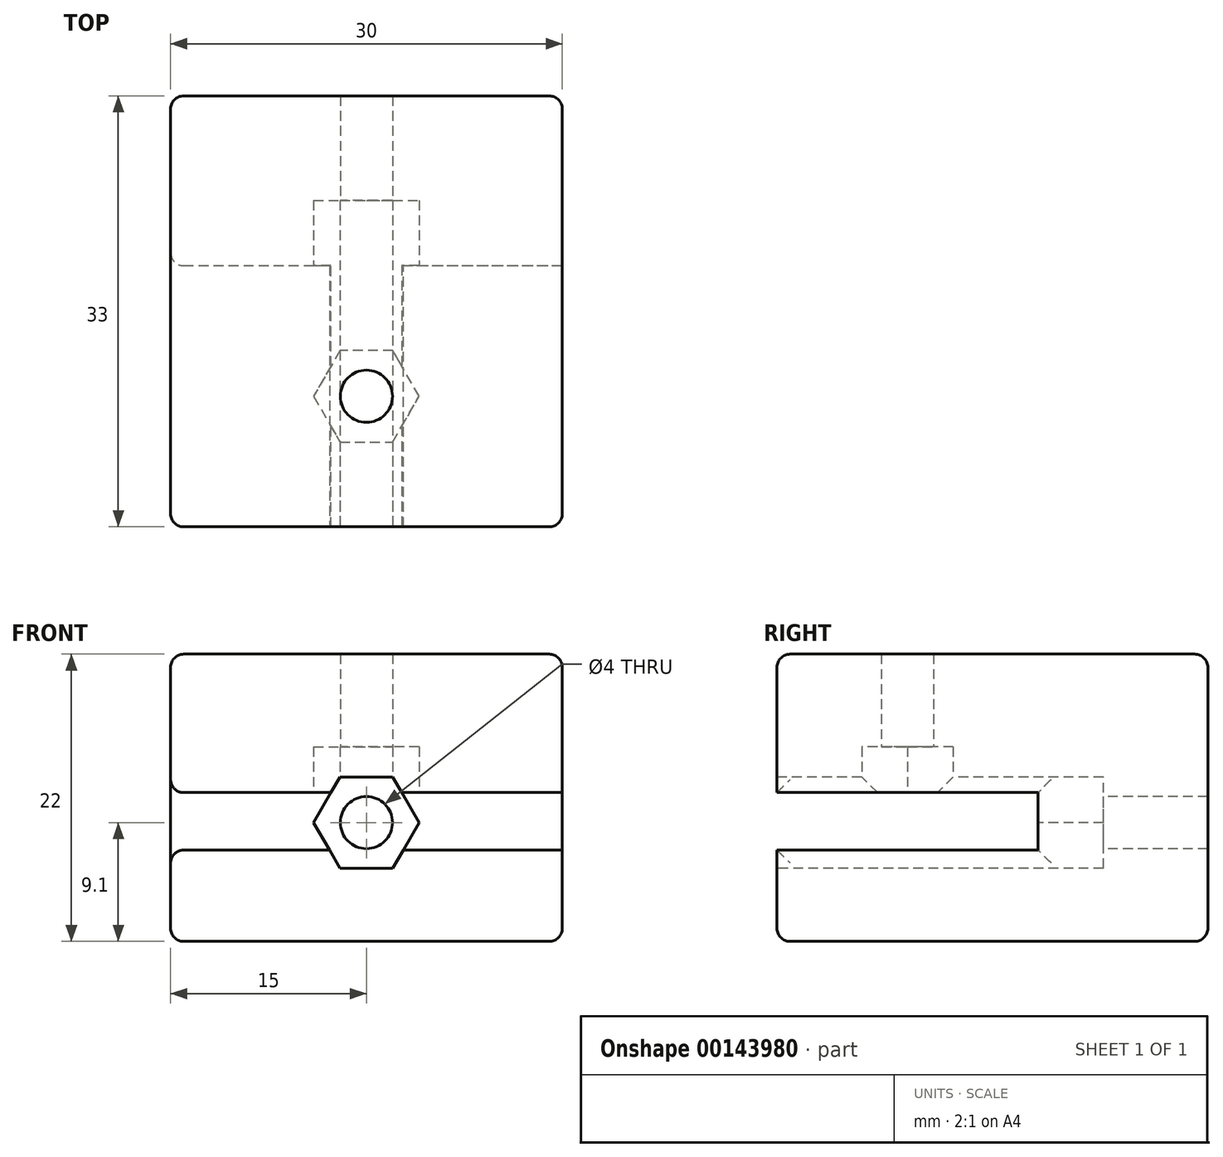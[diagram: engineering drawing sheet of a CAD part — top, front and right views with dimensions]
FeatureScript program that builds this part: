
annotation { "Feature Type Name" : "Feature", "Feature Type Description" : "" }
export const myFeature = defineFeature(function(context is Context, id is Id, definition is map)
    precondition{}
    {
        {
            var Q0;
            Q0=qCreatedBy(makeId("Top.planeOp"),FACE);
            var sketch = newSketch(context, id + "F0", { "sketchPlane" : qUnion([Q0])});
            skLineSegment(sketch, "E0.bottom", {"start": v(-15, 16.5) * mm, "end": v(15, 16.5) * mm});
            skLineSegment(sketch, "E0.top", {"start": v(-15, -16.5) * mm, "end": v(15, -16.5) * mm});
            skLineSegment(sketch, "E0.left", {"start": v(-15, 16.5) * mm, "end": v(-15, -16.5) * mm});
            skLineSegment(sketch, "E0.right", {"start": v(15, 16.5) * mm, "end": v(15, -16.5) * mm});
            skSolve(sketch);
        }
        {
            var Q0;
            Q0=makeQuery(id+"F0.imprint","IMPRINT",FACE,{"disambiguationData":[TD([[makeQuery(id+"F0.imprint","IMPRINT",EDGE,{"derivedFrom":sQuery(id+"F0.wireOp",EDGE,"E0.bottom")}),-1.0]])]});
            extrude(context, id + "F1", {"entities" : qUnion([Q0]), "depth" : 22 * mm});
        }
        {
            var Q0;
            Q0=makeQuery(id+"F1.opExtrude","SWEPT_FACE",FACE,{"disambiguationData":[OSD([sQuery(id+"F0.wireOp",EDGE,"E0.right")])]});
            var sketch = newSketch(context, id + "F2", { "sketchPlane" : qUnion([Q0])});
            skLineSegment(sketch, "E1", {"start": v(-16.5, 7) * mm, "end": v(3.5, 7) * mm});
            skLineSegment(sketch, "E2", {"start": v(3.5, 7) * mm, "end": v(3.5, 11.4) * mm});
            skLineSegment(sketch, "E3", {"start": v(3.5, 11.4) * mm, "end": v(-16.5, 11.4) * mm});
            skSolve(sketch);
        }
        {
            var Q0;
            {var subQ0=sQuery(id+"F2.wireOp",EDGE,"E1");Q0=makeQuery(id+"F2.imprint","IMPRINT",FACE,{"disambiguationData":[TD([[makeQuery(id+"F2.imprint","IMPRINT",EDGE,{"derivedFrom":subQ0}),1.0]])]});}
            extrude(context, id + "F3", {"entities" : qUnion([Q0]), "operationType" : NewBodyOperationType.REMOVE, "endBound" : BoundingType.THROUGH_ALL, "oppositeDirection" : true, "depth" : 25 * mm});
        }
        {
            var Q0;
            Q0=makeQuery(id+"F3.boolean.opBoolean","COPY",FACE,{"derivedFrom":makeQuery(id+"F3.opExtrude","SWEPT_FACE",FACE,{"disambiguationData":[OSD([sQuery(id+"F2.wireOp",EDGE,"E2")])]})});
            var sketch = newSketch(context, id + "F4", { "sketchPlane" : qUnion([Q0])});
            skPoint(sketch, "E4", {"position": v(0, 9.1) * mm});
            skCircle(sketch, "E5.cCircle", {"center": v(0, 9.1) * mm, "radius": 3.5 * mm, "construction": true});
            skLineSegment(sketch, "E5.0", {"start": v(2.02, 5.6) * mm, "end": v(-2.02, 5.6) * mm});
            skLineSegment(sketch, "E5.1", {"start": v(-2.02, 5.6) * mm, "end": v(-4.04, 9.1) * mm});
            skLineSegment(sketch, "E5.2", {"start": v(-4.04, 9.1) * mm, "end": v(-2.02, 12.6) * mm});
            skLineSegment(sketch, "E5.3", {"start": v(-2.02, 12.6) * mm, "end": v(2.02, 12.6) * mm});
            skLineSegment(sketch, "E5.4", {"start": v(2.02, 12.6) * mm, "end": v(4.04, 9.1) * mm});
            skLineSegment(sketch, "E5.5", {"start": v(4.04, 9.1) * mm, "end": v(2.02, 5.6) * mm});
            skPoint(sketch, "E5.0.midPoint", {"position": v(0, 5.6) * mm});
            skCircle(sketch, "E6", {"center": v(0, 9.1) * mm, "radius": 2 * mm});
            skSolve(sketch);
        }
        {
            var Q0;
            {var subQ0=sQuery(id+"F4.wireOp",EDGE,"E5.3");Q0=makeQuery(id+"F4.imprint","IMPRINT",FACE,{"disambiguationData":[TD([[makeQuery(id+"F4.imprint","IMPRINT",EDGE,{"derivedFrom":subQ0}),-1.0]])]});}
            var Q1;
            {var subQ8=sQuery(id+"F4.wireOp",EDGE,"E5.2");var subQ9=sQuery(id+"F4.wireOp",EDGE,"E5.1");var subQ10=makeQuery(id+"F4.imprint","INTERSECT",VERTEX,{"derivedFrom":[subQ9,subQ8]});Q1=makeQuery(id+"F4.imprint","IMPRINT",FACE,{"disambiguationData":[TD([[makeQuery(id+"F4.imprint","IMPRINT",EDGE,{"disambiguationData":[TD([[subQ10,1.0]])],"derivedFrom":subQ9}),-1.0]])]});}
            var Q2;
            {var subQ0=sQuery(id+"F4.wireOp",EDGE,"E5.0");Q2=makeQuery(id+"F4.imprint","IMPRINT",FACE,{"disambiguationData":[TD([[makeQuery(id+"F4.imprint","IMPRINT",EDGE,{"derivedFrom":subQ0}),-1.0]])]});}
            extrude(context, id + "F5", {"entities" : qUnion([Q0, Q1, Q2]), "operationType" : NewBodyOperationType.REMOVE, "oppositeDirection" : true, "depth" : 5 * mm, "hasSecondDirection" : true, "secondDirectionBound" : BoundingType.THROUGH_ALL, "secondDirectionOppositeDirection" : false, "secondDirectionDepth" : 25 * mm});
        }
        {
            var Q0;
            Q0=makeQuery(id+"F5.boolean.opBoolean","SPLIT",FACE,{"disambiguationData":[TD([makeQuery(id+"F5.opExtrude","SWEPT_FACE",FACE,{"disambiguationData":[OSD([sQuery(id+"F4.wireOp",EDGE,"E6")])]})])],"derivedFrom":makeQuery(id+"F3.boolean.opBoolean","COPY",FACE,{"derivedFrom":makeQuery(id+"F3.opExtrude","SWEPT_FACE",FACE,{"disambiguationData":[OSD([sQuery(id+"F2.wireOp",EDGE,"E2")])]})})});
            extrude(context, id + "F6", {"entities" : qUnion([Q0]), "operationType" : NewBodyOperationType.REMOVE, "endBound" : BoundingType.THROUGH_ALL, "oppositeDirection" : true, "depth" : 25 * mm});
        }
        {
            var Q0;
            Q0=makeQuery(id+"F5.boolean.opBoolean","SPLIT",FACE,{"disambiguationData":[TD([makeQuery(id+"F1.opExtrude","SWEPT_FACE",FACE,{"disambiguationData":[OSD([sQuery(id+"F0.wireOp",EDGE,"E0.left")])]})])],"derivedFrom":makeQuery(id+"F3.boolean.opBoolean","COPY",FACE,{"derivedFrom":makeQuery(id+"F3.opExtrude","SWEPT_FACE",FACE,{"disambiguationData":[OSD([sQuery(id+"F2.wireOp",EDGE,"E3")])]})})});
            var sketch = newSketch(context, id + "F7", { "sketchPlane" : qUnion([Q0])});
            skPoint(sketch, "E7", {"position": v(0, 6.5) * mm});
            skLineSegment(sketch, "E8.0.0", {"start": v(-2.71, -3.5) * mm, "end": v(-2.71, 16.5) * mm});
            skLineSegment(sketch, "E8.0.1", {"start": v(-2.71, 16.5) * mm, "end": v(-15, 16.5) * mm});
            skLineSegment(sketch, "E8.0.2", {"start": v(-15, 16.5) * mm, "end": v(-15, -3.5) * mm});
            skLineSegment(sketch, "E8.0.3", {"start": v(-15, -3.5) * mm, "end": v(-2.71, -3.5) * mm});
            skLineSegment(sketch, "E9.0.0", {"start": v(2.71, 16.5) * mm, "end": v(2.71, -3.5) * mm});
            skLineSegment(sketch, "E9.0.1", {"start": v(2.71, -3.5) * mm, "end": v(15, -3.5) * mm});
            skLineSegment(sketch, "E9.0.2", {"start": v(15, -3.5) * mm, "end": v(15, 16.5) * mm});
            skLineSegment(sketch, "E9.0.3", {"start": v(15, 16.5) * mm, "end": v(2.71, 16.5) * mm});
            skCircle(sketch, "E10", {"center": v(0, 6.5) * mm, "radius": 2 * mm});
            skCircle(sketch, "E11.cCircle", {"center": v(0, 6.5) * mm, "radius": 3.5 * mm, "construction": true});
            skLineSegment(sketch, "E11.0", {"start": v(2.02, 3) * mm, "end": v(-2.02, 3) * mm});
            skLineSegment(sketch, "E11.1", {"start": v(-2.02, 3) * mm, "end": v(-4.04, 6.5) * mm});
            skLineSegment(sketch, "E11.2", {"start": v(-4.04, 6.5) * mm, "end": v(-2.02, 10) * mm});
            skLineSegment(sketch, "E11.3", {"start": v(-2.02, 10) * mm, "end": v(2.02, 10) * mm});
            skLineSegment(sketch, "E11.4", {"start": v(2.02, 10) * mm, "end": v(4.04, 6.5) * mm});
            skLineSegment(sketch, "E11.5", {"start": v(4.04, 6.5) * mm, "end": v(2.02, 3) * mm});
            skPoint(sketch, "E11.0.midPoint", {"position": v(0, 3) * mm});
            skSolve(sketch);
        }
        {
            var Q0;
            Q0=makeQuery(id+"F7.imprint","IMPRINT",FACE,{"disambiguationData":[TD([[makeQuery(id+"F7.imprint","IMPRINT",EDGE,{"derivedFrom":sQuery(id+"F7.wireOp",EDGE,"E10")}),1.0]])]});
            extrude(context, id + "F8", {"entities" : qUnion([Q0]), "operationType" : NewBodyOperationType.REMOVE, "endBound" : BoundingType.THROUGH_ALL, "oppositeDirection" : true, "depth" : 25 * mm});
        }
        {
            var Q0;
            Q0=makeQuery(id+"F7.imprint","IMPRINT",FACE,{"disambiguationData":[TD([[makeQuery(id+"F7.imprint","IMPRINT",EDGE,{"derivedFrom":sQuery(id+"F7.wireOp",EDGE,"E10")}),-1.0]])]});
            var Q1;
            {var subQ0=sQuery(id+"F7.wireOp",EDGE,"E11.2");var subQ1=sQuery(id+"F7.wireOp",EDGE,"E8.0.0");var subQ2=makeQuery(id+"F7.imprint","INTERSECT",VERTEX,{"derivedFrom":[subQ1,subQ0]});Q1=makeQuery(id+"F7.imprint","IMPRINT",FACE,{"disambiguationData":[TD([[makeQuery(id+"F7.imprint","IMPRINT",EDGE,{"disambiguationData":[TD([[subQ2,-1.0]])],"derivedFrom":subQ1}),-1.0]])]});}
            var Q2;
            {var subQ0=sQuery(id+"F7.wireOp",EDGE,"E11.4");var subQ1=sQuery(id+"F7.wireOp",EDGE,"E9.0.0");var subQ2=makeQuery(id+"F7.imprint","INTERSECT",VERTEX,{"derivedFrom":[subQ1,subQ0]});Q2=makeQuery(id+"F7.imprint","IMPRINT",FACE,{"disambiguationData":[TD([[makeQuery(id+"F7.imprint","IMPRINT",EDGE,{"disambiguationData":[TD([[subQ2,-1.0]])],"derivedFrom":subQ1}),1.0]])]});}
            extrude(context, id + "F9", {"entities" : qUnion([Q0, Q1, Q2]), "operationType" : NewBodyOperationType.REMOVE, "oppositeDirection" : true, "depth" : 3.5 * mm});
        }
        {
            var Q0;
            Q0=makeQuery(id+"F1.opExtrude","CAP_EDGE",EDGE,{"disambiguationData":[OSD([sQuery(id+"F0.wireOp",EDGE,"E0.bottom")])],"isStart":true});
            var Q1;
            Q1=makeQuery(id+"F1.opExtrude","SWEPT_EDGE",EDGE,{"disambiguationData":[OSD([sQuery(id+"F0.wireOp",EDGE,"E0.bottom"),sQuery(id+"F0.wireOp",EDGE,"E0.right")])]});
            var Q2;
            Q2=makeQuery(id+"F1.opExtrude","CAP_EDGE",EDGE,{"disambiguationData":[OSD([sQuery(id+"F0.wireOp",EDGE,"E0.bottom")])],"isStart":false});
            var Q3;
            Q3=makeQuery(id+"F1.opExtrude","SWEPT_EDGE",EDGE,{"disambiguationData":[OSD([sQuery(id+"F0.wireOp",EDGE,"E0.bottom"),sQuery(id+"F0.wireOp",EDGE,"E0.left")])]});
            var Q4;
            Q4=makeQuery(id+"F1.opExtrude","CAP_EDGE",EDGE,{"disambiguationData":[OSD([sQuery(id+"F0.wireOp",EDGE,"E0.left")])],"isStart":true});
            var Q5;
            Q5=makeQuery(id+"F1.opExtrude","CAP_EDGE",EDGE,{"disambiguationData":[OSD([sQuery(id+"F0.wireOp",EDGE,"E0.top")])],"isStart":true});
            var Q6;
            Q6=makeQuery(id+"F1.opExtrude","CAP_EDGE",EDGE,{"disambiguationData":[OSD([sQuery(id+"F0.wireOp",EDGE,"E0.right")])],"isStart":true});
            var Q7;
            Q7=makeQuery(id+"F1.opExtrude","CAP_EDGE",EDGE,{"disambiguationData":[OSD([sQuery(id+"F0.wireOp",EDGE,"E0.left")])],"isStart":false});
            var Q8;
            Q8=makeQuery(id+"F1.opExtrude","CAP_EDGE",EDGE,{"disambiguationData":[OSD([sQuery(id+"F0.wireOp",EDGE,"E0.top")])],"isStart":false});
            var Q9;
            Q9=makeQuery(id+"F1.opExtrude","CAP_EDGE",EDGE,{"disambiguationData":[OSD([sQuery(id+"F0.wireOp",EDGE,"E0.right")])],"isStart":false});
            var Q10;
            {var subQ0=sQuery(id+"F0.wireOp",EDGE,"E0.left");var subQ1=sQuery(id+"F0.wireOp",EDGE,"E0.top");Q10=makeQuery(id+"F3.boolean.opBoolean","SPLIT",EDGE,{"disambiguationData":[TD([makeQuery(id+"F3.opExtrude","SWEPT_FACE",FACE,{"disambiguationData":[OSD([sQuery(id+"F2.wireOp",EDGE,"E1")])]})])],"derivedFrom":makeQuery(id+"F1.opExtrude","SWEPT_EDGE",EDGE,{"disambiguationData":[OSD([subQ1,subQ0])]})});}
            var Q11;
            {var subQ0=sQuery(id+"F0.wireOp",EDGE,"E0.left");var subQ1=sQuery(id+"F0.wireOp",EDGE,"E0.top");Q11=makeQuery(id+"F3.boolean.opBoolean","SPLIT",EDGE,{"disambiguationData":[TD([makeQuery(id+"F3.opExtrude","SWEPT_FACE",FACE,{"disambiguationData":[OSD([sQuery(id+"F2.wireOp",EDGE,"E3")])]})])],"derivedFrom":makeQuery(id+"F1.opExtrude","SWEPT_EDGE",EDGE,{"disambiguationData":[OSD([subQ1,subQ0])]})});}
            var Q12;
            {var subQ0=sQuery(id+"F0.wireOp",EDGE,"E0.right");var subQ1=sQuery(id+"F0.wireOp",EDGE,"E0.top");Q12=makeQuery(id+"F3.boolean.opBoolean","SPLIT",EDGE,{"disambiguationData":[TD([makeQuery(id+"F3.opExtrude","SWEPT_FACE",FACE,{"disambiguationData":[OSD([sQuery(id+"F2.wireOp",EDGE,"E1")])]})])],"derivedFrom":makeQuery(id+"F1.opExtrude","SWEPT_EDGE",EDGE,{"disambiguationData":[OSD([subQ1,subQ0])]})});}
            var Q13;
            {var subQ0=sQuery(id+"F0.wireOp",EDGE,"E0.right");var subQ1=sQuery(id+"F0.wireOp",EDGE,"E0.top");Q13=makeQuery(id+"F3.boolean.opBoolean","SPLIT",EDGE,{"disambiguationData":[TD([makeQuery(id+"F3.opExtrude","SWEPT_FACE",FACE,{"disambiguationData":[OSD([sQuery(id+"F2.wireOp",EDGE,"E3")])]})])],"derivedFrom":makeQuery(id+"F1.opExtrude","SWEPT_EDGE",EDGE,{"disambiguationData":[OSD([subQ1,subQ0])]})});}
            var Q14;
            Q14=makeQuery(id+"F3.boolean.opBoolean","COPY",EDGE,{"derivedFrom":makeQuery(id+"F3.opExtrude","CAP_EDGE",EDGE,{"disambiguationData":[OSD([sQuery(id+"F2.wireOp",EDGE,"E3")])],"isStart":true})});
            var Q15;
            Q15=makeQuery(id+"F3.boolean.opBoolean","COPY",EDGE,{"derivedFrom":makeQuery(id+"F3.opExtrude","CAP_EDGE",EDGE,{"disambiguationData":[OSD([sQuery(id+"F2.wireOp",EDGE,"E1")])],"isStart":true})});
            var Q16;
            {var subQ0=sQuery(id+"F0.wireOp",EDGE,"E0.top");var subQ1=sQuery(id+"F0.wireOp",EDGE,"E0.right");var subQ2=sQuery(id+"F2.wireOp",EDGE,"E1");Q16=makeQuery(id+"F5.boolean.opBoolean","SPLIT",EDGE,{"disambiguationData":[TD([makeQuery(id+"F1.opExtrude","SWEPT_FACE",FACE,{"disambiguationData":[OSD([subQ1])]})])],"derivedFrom":makeQuery(id+"F3.boolean.opBoolean","COPY",EDGE,{"derivedFrom":makeQuery(id+"F3.opExtrude","SWEPT_EDGE",EDGE,{"disambiguationData":[OSD([subQ0,subQ1,subQ2])]})})});}
            var Q17;
            {var subQ0=sQuery(id+"F0.wireOp",EDGE,"E0.top");var subQ1=sQuery(id+"F2.wireOp",EDGE,"E1");Q17=makeQuery(id+"F5.boolean.opBoolean","SPLIT",EDGE,{"disambiguationData":[TD([makeQuery(id+"F1.opExtrude","SWEPT_FACE",FACE,{"disambiguationData":[OSD([sQuery(id+"F0.wireOp",EDGE,"E0.left")])]})])],"derivedFrom":makeQuery(id+"F3.boolean.opBoolean","COPY",EDGE,{"derivedFrom":makeQuery(id+"F3.opExtrude","SWEPT_EDGE",EDGE,{"disambiguationData":[OSD([subQ0,sQuery(id+"F0.wireOp",EDGE,"E0.right"),subQ1])]})})});}
            var Q18;
            {var subQ0=sQuery(id+"F0.wireOp",EDGE,"E0.top");var subQ1=sQuery(id+"F2.wireOp",EDGE,"E3");Q18=makeQuery(id+"F5.boolean.opBoolean","SPLIT",EDGE,{"disambiguationData":[TD([makeQuery(id+"F1.opExtrude","SWEPT_FACE",FACE,{"disambiguationData":[OSD([sQuery(id+"F0.wireOp",EDGE,"E0.left")])]})])],"derivedFrom":makeQuery(id+"F3.boolean.opBoolean","COPY",EDGE,{"derivedFrom":makeQuery(id+"F3.opExtrude","SWEPT_EDGE",EDGE,{"disambiguationData":[OSD([subQ0,sQuery(id+"F0.wireOp",EDGE,"E0.right"),subQ1])]})})});}
            var Q19;
            Q19=makeQuery(id+"F3.boolean.opBoolean","INTERSECT",EDGE,{"derivedFrom":[makeQuery(id+"F1.opExtrude","SWEPT_FACE",FACE,{"disambiguationData":[OSD([sQuery(id+"F0.wireOp",EDGE,"E0.left")])]}),makeQuery(id+"F3.opExtrude","SWEPT_FACE",FACE,{"disambiguationData":[OSD([sQuery(id+"F2.wireOp",EDGE,"E2")])]})]});
            var Q20;
            Q20=makeQuery(id+"F3.boolean.opBoolean","INTERSECT",EDGE,{"derivedFrom":[makeQuery(id+"F1.opExtrude","SWEPT_FACE",FACE,{"disambiguationData":[OSD([sQuery(id+"F0.wireOp",EDGE,"E0.left")])]}),makeQuery(id+"F3.opExtrude","SWEPT_FACE",FACE,{"disambiguationData":[OSD([sQuery(id+"F2.wireOp",EDGE,"E1")])]})]});
            var Q21;
            Q21=makeQuery(id+"F3.boolean.opBoolean","INTERSECT",EDGE,{"derivedFrom":[makeQuery(id+"F1.opExtrude","SWEPT_FACE",FACE,{"disambiguationData":[OSD([sQuery(id+"F0.wireOp",EDGE,"E0.left")])]}),makeQuery(id+"F3.opExtrude","SWEPT_FACE",FACE,{"disambiguationData":[OSD([sQuery(id+"F2.wireOp",EDGE,"E3")])]})]});
            var Q22;
            Q22=makeQuery(id+"F3.boolean.opBoolean","COPY",EDGE,{"derivedFrom":makeQuery(id+"F3.opExtrude","CAP_EDGE",EDGE,{"disambiguationData":[OSD([sQuery(id+"F2.wireOp",EDGE,"E2")])],"isStart":true})});
            fillet(context, id + "F10", {"entities" : qUnion([Q0, Q1, Q2, Q3, Q4, Q5, Q6, Q7, Q8, Q9, Q10, Q11, Q12, Q13, Q14, Q15, Q16, Q17, Q18, Q19, Q20, Q21, Q22]), "radius" : 1 * mm, "tangentPropagation" : true, "defaultsChanged" : false, "vertexSettings" : [], "allowEdgeOverflow" : false});
        }
    });
